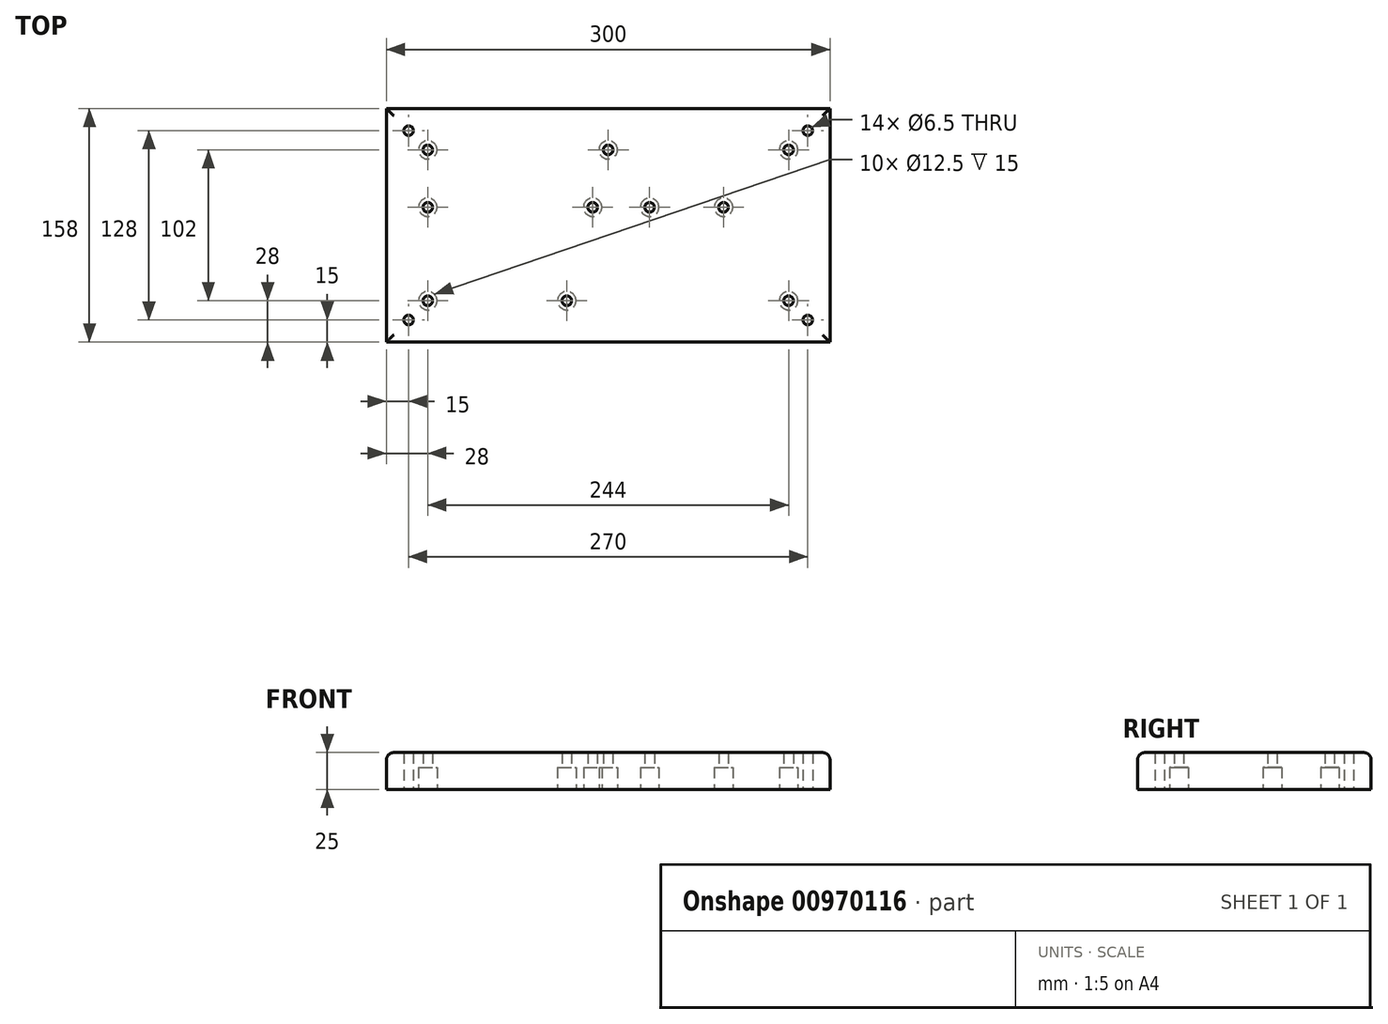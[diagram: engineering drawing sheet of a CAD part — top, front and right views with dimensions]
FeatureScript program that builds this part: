
annotation { "Feature Type Name" : "Feature", "Feature Type Description" : "" }
export const myFeature = defineFeature(function(context is Context, id is Id, definition is map)
    precondition{}
    {
        {
            var Q0;
            Q0=qCreatedBy(makeId("Top.planeOp"),FACE);
            var sketch = newSketch(context, id + "F0", { "sketchPlane" : qUnion([Q0])});
            skLineSegment(sketch, "E0.bottom", {"start": v(0, 0) * mm, "end": v(300, 0) * mm});
            skLineSegment(sketch, "E0.top", {"start": v(0, 158) * mm, "end": v(300, 158) * mm});
            skLineSegment(sketch, "E0.left", {"start": v(0, 0) * mm, "end": v(0, 158) * mm});
            skLineSegment(sketch, "E0.right", {"start": v(300, 0) * mm, "end": v(300, 158) * mm});
            skSolve(sketch);
        }
        {
            var Q0;
            Q0 = qSketchRegion(id + "F0", true);
            extrude(context, id + "F1", {"entities" : qUnion([Q0]), "depth" : 25 * mm, "offsetDistance" : 25 * mm});
        }
        {
            var Q0;
            Q0=makeQuery(id+"F1.opExtrude","CAP_EDGE",EDGE,{"disambiguationData":[OSD([sQuery(id+"F0.wireOp",EDGE,"E0.left")])],"isStart":false});
            var Q1;
            Q1=makeQuery(id+"F1.opExtrude","CAP_EDGE",EDGE,{"disambiguationData":[OSD([sQuery(id+"F0.wireOp",EDGE,"E0.top")])],"isStart":false});
            var Q2;
            Q2=makeQuery(id+"F1.opExtrude","CAP_EDGE",EDGE,{"disambiguationData":[OSD([sQuery(id+"F0.wireOp",EDGE,"E0.bottom")])],"isStart":false});
            var Q3;
            Q3=makeQuery(id+"F1.opExtrude","CAP_EDGE",EDGE,{"disambiguationData":[OSD([sQuery(id+"F0.wireOp",EDGE,"E0.right")])],"isStart":false});
            fillet(context, id + "F2", {"entities" : qUnion([Q0, Q1, Q2, Q3]), "radius" : 5 * mm, "tangentPropagation" : true, "allowEdgeOverflow" : false});
        }
        {
            var Q0;
            Q0=makeQuery(id+"F1.opExtrude","CAP_FACE",FACE,{"disambiguationData":[OSD([sQuery(id+"F0.wireOp",EDGE,"E0.bottom"),sQuery(id+"F0.wireOp",EDGE,"E0.top"),sQuery(id+"F0.wireOp",EDGE,"E0.left"),sQuery(id+"F0.wireOp",EDGE,"E0.right")])],"isStart":true});
            var sketch = newSketch(context, id + "F3", { "sketchPlane" : qUnion([Q0])});
            skCircle(sketch, "E1", {"center": v(15, -15) * mm, "radius": 3.25 * mm});
            skLineSegment(sketch, "E2", {"start": v(150, 0) * mm, "end": v(150, -158) * mm, "construction": true});
            skLineSegment(sketch, "E3", {"start": v(0, -79) * mm, "end": v(300, -79) * mm, "construction": true});
            skCircle(sketch, "E4.MirrorC", {"center": v(285, -15) * mm, "radius": 3.25 * mm});
            skCircle(sketch, "E5.MirrorC", {"center": v(15, -143) * mm, "radius": 3.25 * mm});
            skCircle(sketch, "E6.MirrorC", {"center": v(285, -143) * mm, "radius": 3.25 * mm});
            skSolve(sketch);
        }
        {
            var Q0;
            Q0 = qSketchRegion(id + "F3", true);
            extrude(context, id + "F4", {"entities" : qUnion([Q0]), "operationType" : NewBodyOperationType.REMOVE, "oppositeDirection" : true, "depth" : 25 * mm, "offsetDistance" : 25 * mm});
        }
        {
            var Q0;
            Q0=makeQuery(id+"F1.opExtrude","CAP_FACE",FACE,{"disambiguationData":[OSD([sQuery(id+"F0.wireOp",EDGE,"E0.bottom"),sQuery(id+"F0.wireOp",EDGE,"E0.top"),sQuery(id+"F0.wireOp",EDGE,"E0.left"),sQuery(id+"F0.wireOp",EDGE,"E0.right")])],"isStart":true});
            var sketch = newSketch(context, id + "F5", { "sketchPlane" : qUnion([Q0])});
            skLineSegment(sketch, "E7", {"start": v(0, -79) * mm, "end": v(300, -79) * mm, "construction": true});
            skLineSegment(sketch, "E8", {"start": v(150, 0) * mm, "end": v(150, -158) * mm, "construction": true});
            skCircle(sketch, "E9", {"center": v(272, -28) * mm, "radius": 3.25 * mm});
            skCircle(sketch, "E10.MirrorC", {"center": v(28, -28) * mm, "radius": 3.25 * mm});
            skCircle(sketch, "E11.MirrorC", {"center": v(28, -130) * mm, "radius": 3.25 * mm});
            skCircle(sketch, "E12.MirrorC", {"center": v(272, -130) * mm, "radius": 3.25 * mm});
            skCircle(sketch, "E13", {"center": v(150, -130) * mm, "radius": 3.25 * mm});
            skCircle(sketch, "E14", {"center": v(122, -28) * mm, "radius": 3.25 * mm});
            skLineSegment(sketch, "E15", {"start": v(0, -91.2) * mm, "end": v(300, -91.2) * mm, "construction": true});
            skCircle(sketch, "E16", {"center": v(28, -91.2) * mm, "radius": 3.25 * mm});
            skCircle(sketch, "E17", {"center": v(139.5, -91.2) * mm, "radius": 3.25 * mm});
            skCircle(sketch, "E18", {"center": v(178, -91.2) * mm, "radius": 3.25 * mm});
            skCircle(sketch, "E19", {"center": v(228, -91.2) * mm, "radius": 3.25 * mm});
            skSolve(sketch);
        }
        {
            var Q0;
            Q0 = qSketchRegion(id + "F5", true);
            extrude(context, id + "F6", {"entities" : qUnion([Q0]), "operationType" : NewBodyOperationType.REMOVE, "oppositeDirection" : true, "depth" : 25 * mm, "offsetDistance" : 25 * mm});
        }
        {
            var Q0;
            Q0=makeQuery(id+"F1.opExtrude","CAP_FACE",FACE,{"disambiguationData":[OSD([sQuery(id+"F0.wireOp",EDGE,"E0.bottom"),sQuery(id+"F0.wireOp",EDGE,"E0.top"),sQuery(id+"F0.wireOp",EDGE,"E0.left"),sQuery(id+"F0.wireOp",EDGE,"E0.right")])],"isStart":true});
            var sketch = newSketch(context, id + "F7", { "sketchPlane" : qUnion([Q0])});
            skCircle(sketch, "E20", {"center": v(28, -28) * mm, "radius": 6.25 * mm});
            skCircle(sketch, "E21", {"center": v(122, -28) * mm, "radius": 6.25 * mm});
            skCircle(sketch, "E22", {"center": v(272, -28) * mm, "radius": 6.25 * mm});
            skCircle(sketch, "E23", {"center": v(228, -91.2) * mm, "radius": 6.25 * mm});
            skCircle(sketch, "E24", {"center": v(178, -91.2) * mm, "radius": 6.25 * mm});
            skCircle(sketch, "E25", {"center": v(139.5, -91.2) * mm, "radius": 6.25 * mm});
            skCircle(sketch, "E26", {"center": v(150, -130) * mm, "radius": 6.25 * mm});
            skCircle(sketch, "E27", {"center": v(272, -130) * mm, "radius": 6.25 * mm});
            skCircle(sketch, "E28", {"center": v(28, -130) * mm, "radius": 6.25 * mm});
            skCircle(sketch, "E29", {"center": v(28, -91.2) * mm, "radius": 6.25 * mm});
            skSolve(sketch);
        }
        {
            var Q0;
            Q0 = qSketchRegion(id + "F7", true);
            extrude(context, id + "F8", {"entities" : qUnion([Q0]), "operationType" : NewBodyOperationType.REMOVE, "oppositeDirection" : true, "depth" : 15 * mm, "offsetDistance" : 25 * mm});
        }
    });
